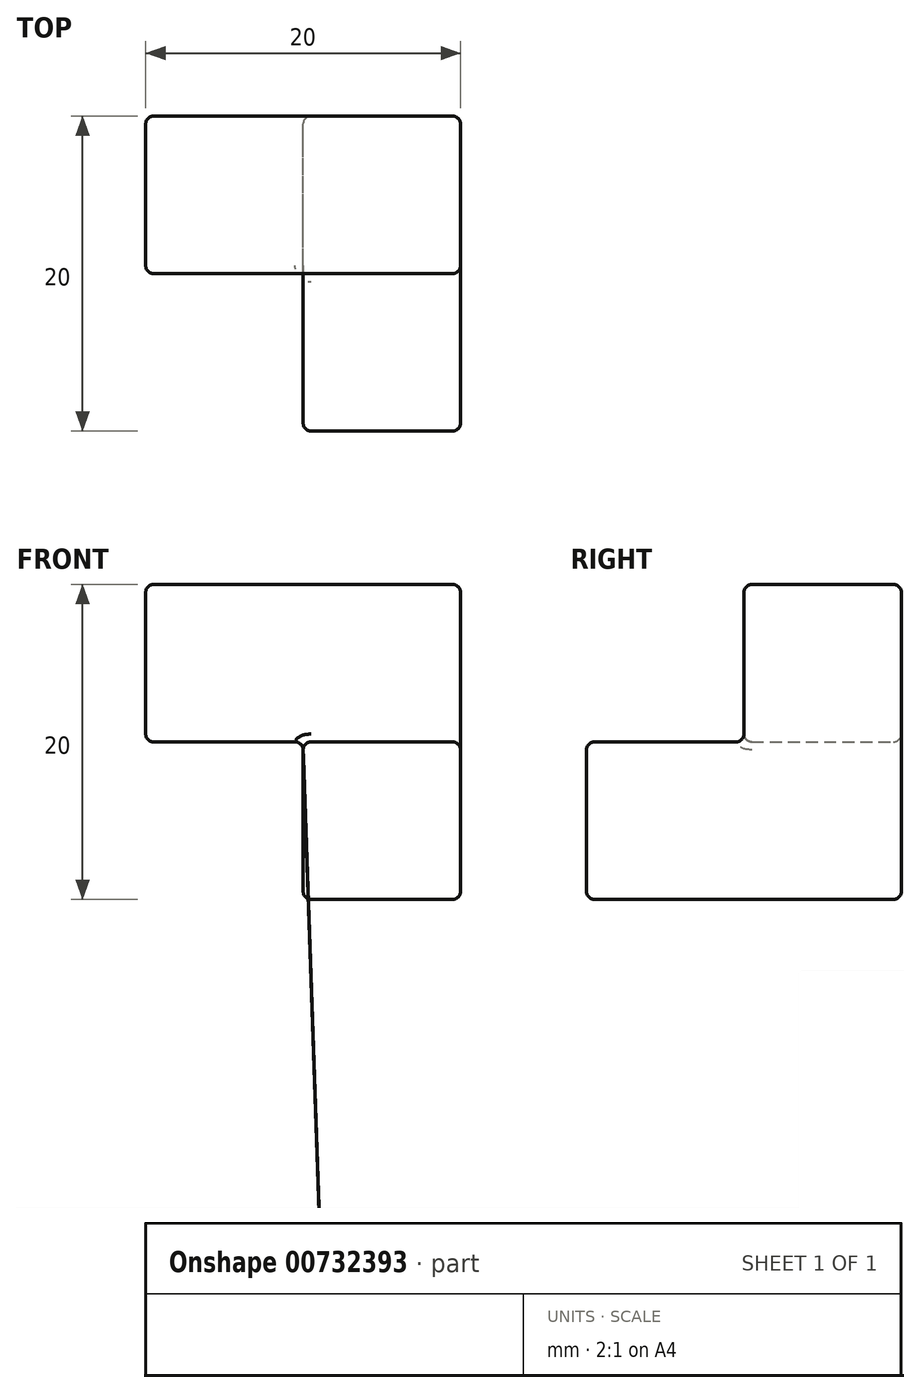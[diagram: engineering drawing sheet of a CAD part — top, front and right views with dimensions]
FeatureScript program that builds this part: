
annotation { "Feature Type Name" : "Feature", "Feature Type Description" : "" }
export const myFeature = defineFeature(function(context is Context, id is Id, definition is map)
    precondition{}
    {
        {
            var Q0;
            Q0=qCreatedBy(makeId("Front.planeOp"),FACE);
            var sketch = newSketch(context, id + "F0", { "sketchPlane" : qUnion([Q0])});
            skLineSegment(sketch, "E0.bottom", {"start": v(-10, -5) * mm, "end": v(10, -5) * mm});
            skLineSegment(sketch, "E0.top", {"start": v(-10, 5) * mm, "end": v(10, 5) * mm});
            skLineSegment(sketch, "E0.left", {"start": v(-10, -5) * mm, "end": v(-10, 5) * mm});
            skLineSegment(sketch, "E0.right", {"start": v(10, -5) * mm, "end": v(10, 5) * mm});
            skPoint(sketch, "E0.middle", {"position": v(0, 0) * mm});
            skLineSegment(sketch, "E1", {"start": v(0, -5) * mm, "end": v(0, -15) * mm});
            skLineSegment(sketch, "E2", {"start": v(0, -15) * mm, "end": v(10, -15) * mm});
            skLineSegment(sketch, "E3", {"start": v(10, -15) * mm, "end": v(10, -5) * mm});
            skSolve(sketch);
        }
        {
            var Q0;
            Q0=makeQuery(id+"F0.imprint","IMPRINT",FACE,{"disambiguationData":[TD([[makeQuery(id+"F0.imprint","IMPRINT",EDGE,{"derivedFrom":sQuery(id+"F0.wireOp",EDGE,"E0.top")}),-1.0]])]});
            extrude(context, id + "F1", {"entities" : qUnion([Q0]), "depth" : 10 * mm, "offsetDistance" : 25 * mm});
        }
        {
            var Q0;
            {var subQ2=sQuery(id+"F0.wireOp",EDGE,"E1");Q0=makeQuery(id+"F0.imprint","IMPRINT",FACE,{"disambiguationData":[TD([[makeQuery(id+"F0.imprint","IMPRINT",EDGE,{"derivedFrom":subQ2}),1.0]])]});}
            extrude(context, id + "F2", {"entities" : qUnion([Q0]), "operationType" : NewBodyOperationType.ADD, "depth" : 20 * mm, "offsetDistance" : 25 * mm});
        }
        {
            var Q0;
            {var subQ0=sQuery(id+"F0.wireOp",EDGE,"E0.bottom");Q0=makeQuery(id+"F2.boolean.opBoolean","MERGE",FACE,{"derivedFrom":[makeQuery(id+"F1.opExtrude","CAP_FACE",FACE,{"disambiguationData":[OSD([subQ0,sQuery(id+"F0.wireOp",EDGE,"E0.top"),sQuery(id+"F0.wireOp",EDGE,"E0.left"),sQuery(id+"F0.wireOp",EDGE,"E0.right")])],"isStart":true}),makeQuery(id+"F2.opExtrude","CAP_FACE",FACE,{"disambiguationData":[OSD([subQ0,sQuery(id+"F0.wireOp",EDGE,"E1"),sQuery(id+"F0.wireOp",EDGE,"E2"),sQuery(id+"F0.wireOp",EDGE,"E3")])],"isStart":true})]});}
            var Q1;
            Q1=makeQuery(id+"F2.boolean.opBoolean","MERGE",FACE,{"derivedFrom":[makeQuery(id+"F1.opExtrude","SWEPT_FACE",FACE,{"disambiguationData":[OSD([sQuery(id+"F0.wireOp",EDGE,"E0.right")])]}),makeQuery(id+"F2.opExtrude","SWEPT_FACE",FACE,{"disambiguationData":[OSD([sQuery(id+"F0.wireOp",EDGE,"E3")])]})]});
            var Q2;
            Q2=makeQuery(id+"F2.opExtrude","SWEPT_FACE",FACE,{"disambiguationData":[OSD([sQuery(id+"F0.wireOp",EDGE,"E1")])]});
            var Q3;
            Q3=makeQuery(id+"F2.opExtrude","CAP_FACE",FACE,{"disambiguationData":[OSD([sQuery(id+"F0.wireOp",EDGE,"E0.bottom"),sQuery(id+"F0.wireOp",EDGE,"E1"),sQuery(id+"F0.wireOp",EDGE,"E2"),sQuery(id+"F0.wireOp",EDGE,"E3")])],"isStart":false});
            var Q4;
            Q4=makeQuery(id+"F1.opExtrude","CAP_FACE",FACE,{"disambiguationData":[OSD([sQuery(id+"F0.wireOp",EDGE,"E0.bottom"),sQuery(id+"F0.wireOp",EDGE,"E0.top"),sQuery(id+"F0.wireOp",EDGE,"E0.left"),sQuery(id+"F0.wireOp",EDGE,"E0.right")])],"isStart":false});
            var Q5;
            Q5=makeQuery(id+"F1.opExtrude","SWEPT_FACE",FACE,{"disambiguationData":[OSD([sQuery(id+"F0.wireOp",EDGE,"E0.left")])]});
            fillet(context, id + "F3", {"entities" : qUnion([Q0, Q1, Q2, Q3, Q4, Q5]), "radius" : 0.5 * mm, "tangentPropagation" : true, "allowEdgeOverflow" : false});
        }
    });
